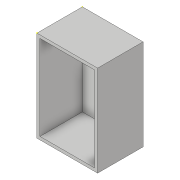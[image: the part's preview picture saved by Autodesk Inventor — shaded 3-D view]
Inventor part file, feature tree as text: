
AUTODESK INVENTOR PART (.ipt)
format: ipt  version: 2019 (Build 230136000, 136)  size: 164,864 bytes
history: native  units: in
note: dims shown in document units (in); Inventor stores cm internally (conversion verified against a paired STEP export)
features: sketch x10, extrude x5, plane x1
ambient origin geometry x8: Origin, YZ Plane, XZ Plane, XY Plane, X Axis, Y Axis, Z Axis, Center Point
bodies: Solid1 (feature_tree)
feature tree (16):
  extrude  "Extrusion1"  Depth=5.9055in
  sketch  "Sketch2"  dims[d2=7.874in d3=0.0in d4=7.4803in]
  sketch  "Sketch3"  dims[d5=11.4173in d6=0.3937in]
  sketch  "Sketch4"  dims[d7=0.3937in d8=5.5118in d9=0.0in]
  extrude  "Extrusion2"  Depth=7.4803in
  plane  "Work Plane1"
  sketch  "Sketch6"  dims[d15=2.9528in]
  extrude  "Extrusion3"  Depth=0.3937in
  extrude  "Extrusion4"  Depth=5.5118in TaperAngle=0.0deg
  sketch  "Sketch9"  dims[d18=3.937in]
  extrude  "Extrusion5"  Depth=1.9685in
  sketch  "Sketch1"  dims[d0=11.811in d1=5.9055in]
  sketch  "Sketch5"  dims[d10=0.0in d14=1.9685in]
  sketch  "Sketch7"  dims[d16=1.9685in]
  sketch  "Sketch8"  dims[d17=0.7874in]
  sketch  "Sketch14"  dims[d19=1.5748in d20=3.937in d21=0.7874in d22=1.9685in d23=0.0in d24=2.9528in d25=1.9685in d26=2.9528in d27=0.7874in d28=1.9685in d29=1.5748in d30=3.937in d31=1.5748in d32=1.9685in d33=1.9685in d34=2.9528in d35=0.7874in d36=1.9685in d37=1.5748in d38=3.937in d39=1.5748in d40=1.9685in d41=2.9528in d42=1.9685in d43=0.7874in d44=1.9685in d45=1.5748in d46=3.937in d47=1.5748in d48=1.9685in d49=1.9685in d50=0.0in d52=3.937in d53=0.3937in d54=0.0in]
